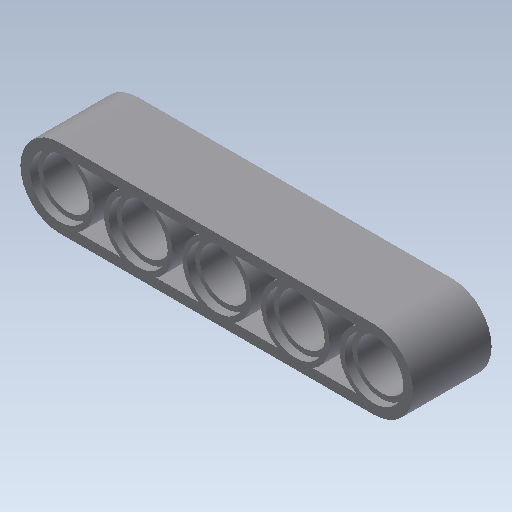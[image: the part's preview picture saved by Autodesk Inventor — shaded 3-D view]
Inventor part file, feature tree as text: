
AUTODESK INVENTOR PART (.ipt)
format: ipt  version: 2020 (Build 240168000, 168)  size: 204,800 bytes
history: native  units: mm
features: extrude x5, sketch x5
ambient origin geometry x8: Origin, YZ Plane, XZ Plane, XY Plane, X Axis, Y Axis, Z Axis, Center Point
bodies: Solid1 (feature_tree)
feature tree (10):
  extrude  "Extrusion1"  Depth=4.0mm
  extrude  "Extrusion2"  Depth=32.0mm
  extrude  "Extrusion3"  Depth=16.0mm
  extrude  "Extrusion4"  Depth=32.0mm
  extrude  "Extrusion5"  Depth=0.8mm
  sketch  "Sketch1"  dims[d3=4.0mm d4=4.0mm]
  sketch  "Sketch2"  dims[d5=32.0mm d6=32.0mm]
  sketch  "Sketch3"  dims[d7=0.0mm d8=16.0mm]
  sketch  "Sketch4"  dims[d9=32.0mm d10=32.0mm]
  sketch  "Sketch5"  dims[d11=8.0mm d12=0.0mm d13=5.0mm d14=10.0mm d16=10.0mm d17=50.0mm d19=8.0mm d21=10.0mm d22=0.0mm d23=6.0mm d24=10.0mm d26=10.0mm d27=50.0mm d29=8.0mm d31=0.8mm d32=0.0mm d33=6.0mm d34=10.0mm d36=10.0mm d37=50.0mm d39=8.0mm d41=0.8mm d42=0.0mm d43=3.5mm d44=3.5mm d45=4.394449mm d46=4.394449mm d47=10.0mm d49=10.0mm d50=40.0mm d52=8.0mm d54=0.8mm d55=0.0mm]
